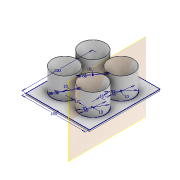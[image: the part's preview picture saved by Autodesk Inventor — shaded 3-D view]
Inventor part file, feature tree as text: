
AUTODESK INVENTOR PART (.ipt)
format: ipt  version: 2020.3 (Build 243373010, 373A)  size: 155,648 bytes
history: native  units: mm
features: sketch x2, plane x1, revolve x1, pattern_linear x1, extrude x1
ambient origin geometry x8: Origin, YZ Plane, XZ Plane, XY Plane, X Axis, Y Axis, Z Axis, Center Point
bodies: Solid1 (feature_tree)
feature tree (6):
  sketch  "Sketch1"  dims[d0=180.0mm d1=200.0mm]
  plane  "Work Plane1"
  revolve  "Revolution1"  [1 undecoded]
  pattern_linear  "Rectangular Pattern1"  Spacing1=10.0mm  [1 undecoded]
  extrude  "Extrusion1"  Depth=10.0mm
  sketch  "Sketch2"  dims[d2=70.0mm d3=70.0mm d4=70.0mm d5=70.0mm d6=10.0mm d7=10.0mm d8=68.0mm d9=68.0mm d10=68.0mm d11=68.0mm d12=10.0mm d13=10.0mm d14=10.0mm d15=10.0mm d16=-50.0mm d17=60.0mm d18=0.0mm d20=90.0deg d21=20.0mm d23=-80.0mm d24=20.0mm d26=80.0mm d27=5.0mm d28=0.0mm]
note: 2 required parameter values undecoded (feature->parameter linkage not recoverable at this tier; creation-order binding heuristic only, values carry confidence <= 0.55)